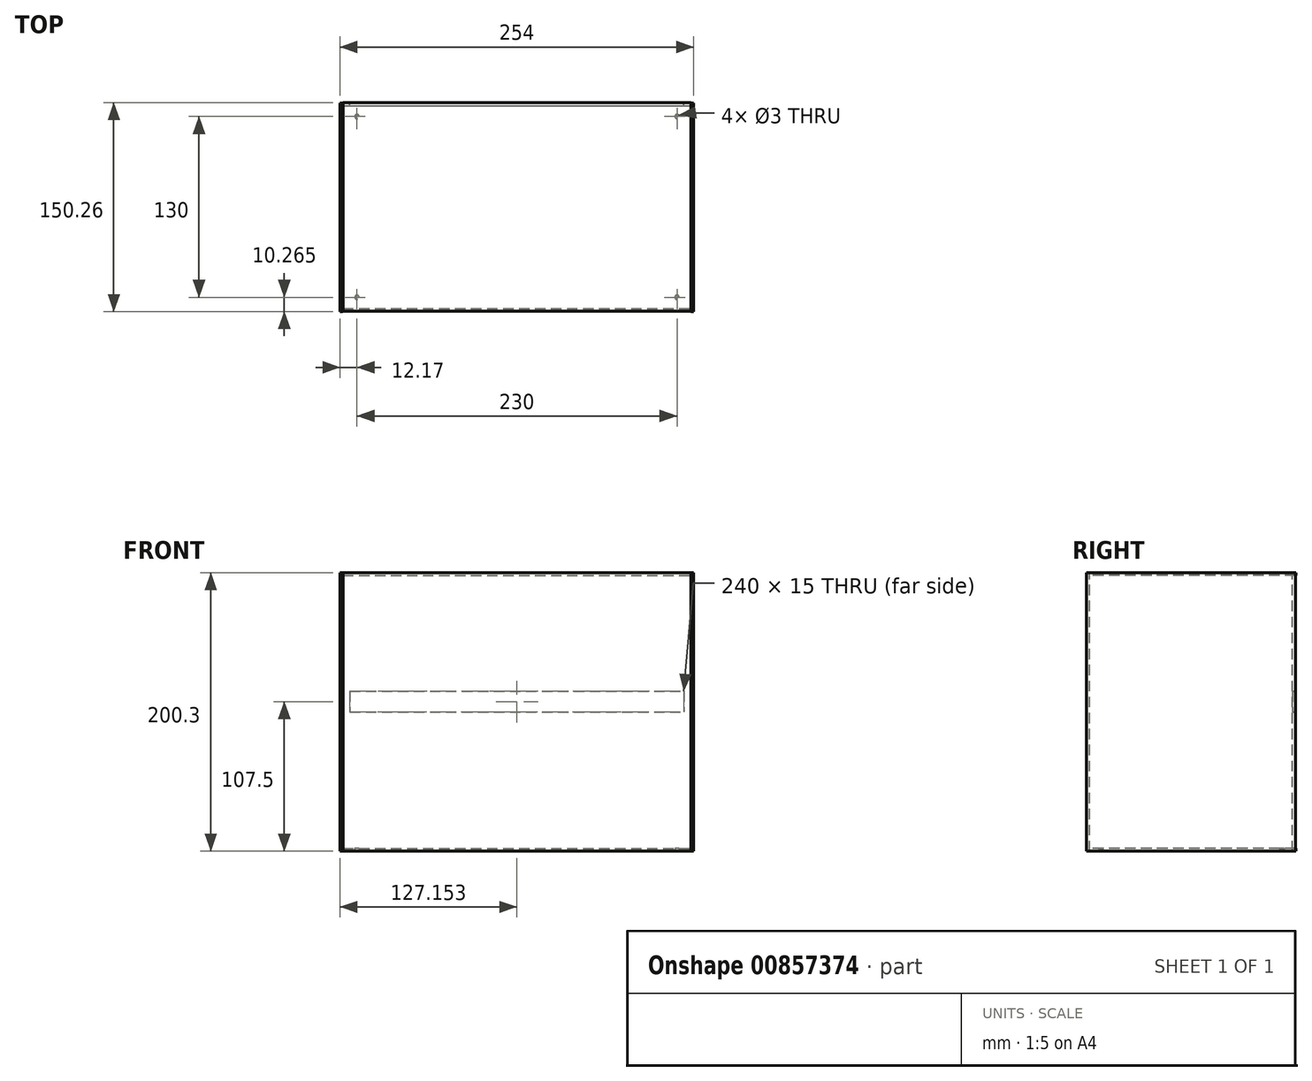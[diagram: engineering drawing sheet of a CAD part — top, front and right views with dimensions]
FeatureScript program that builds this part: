
annotation { "Feature Type Name" : "Feature", "Feature Type Description" : "" }
export const myFeature = defineFeature(function(context is Context, id is Id, definition is map)
    precondition{}
    {
        {
            var Q0;
            Q0=qCreatedBy(makeId("Top.planeOp"),FACE);
            var sketch = newSketch(context, id + "F0", { "sketchPlane" : qUnion([Q0])});
            skLineSegment(sketch, "E0.bottom", {"start": v(-126.83, 77.1) * mm, "end": v(123.17, 77.1) * mm});
            skLineSegment(sketch, "E0.top", {"start": v(-126.83, -72.9) * mm, "end": v(123.17, -72.9) * mm});
            skLineSegment(sketch, "E0.left", {"start": v(-126.83, 77.1) * mm, "end": v(-126.83, -72.9) * mm});
            skLineSegment(sketch, "E0.right", {"start": v(123.17, 77.1) * mm, "end": v(123.17, -72.9) * mm});
            skCircle(sketch, "E1", {"center": v(113.17, -62.9) * mm, "radius": 1.5 * mm});
            skCircle(sketch, "E2", {"center": v(113.17, 67.1) * mm, "radius": 1.5 * mm});
            skCircle(sketch, "E3", {"center": v(-116.83, 67.1) * mm, "radius": 1.5 * mm});
            skCircle(sketch, "E4", {"center": v(-116.83, -62.9) * mm, "radius": 1.5 * mm});
            skSolve(sketch);
        }
        {
            var Q0;
            Q0 = qSketchRegion(id + "F0", true);
            extrude(context, id + "F1", {"entities" : qUnion([Q0]), "depth" : 2 * mm, "offsetDistance" : 25 * mm});
        }
        {
            var Q0;
            Q0=qCreatedBy(makeId("Front.planeOp"),FACE);
            var sketch = newSketch(context, id + "F2", { "sketchPlane" : qUnion([Q0])});
            skLineSegment(sketch, "E5.bottom", {"start": v(-126.85, 0) * mm, "end": v(123.15, 0) * mm});
            skLineSegment(sketch, "E5.top", {"start": v(-126.85, 200) * mm, "end": v(123.15, 200) * mm});
            skLineSegment(sketch, "E5.left", {"start": v(-126.85, 0) * mm, "end": v(-126.85, 200) * mm});
            skLineSegment(sketch, "E5.right", {"start": v(123.15, 0) * mm, "end": v(123.15, 200) * mm});
            skLineSegment(sketch, "E6.bottom", {"start": v(-121.85, 115) * mm, "end": v(118.15, 115) * mm});
            skLineSegment(sketch, "E6.top", {"start": v(-121.85, 100) * mm, "end": v(118.15, 100) * mm});
            skLineSegment(sketch, "E6.left", {"start": v(-121.85, 115) * mm, "end": v(-121.85, 100) * mm});
            skLineSegment(sketch, "E6.right", {"start": v(118.15, 115) * mm, "end": v(118.15, 100) * mm});
            skSolve(sketch);
        }
        {
            var Q0;
            Q0 = qSketchRegion(id + "F2", true);
            extrude(context, id + "F3", {"entities" : qUnion([Q0]), "depth" : 2 * mm, "offsetDistance" : 25 * mm});
        }
        {
            var Q0;
            Q0=makeQuery(id+"F3.opExtrude","SWEPT_BODY",BODY,{"disambiguationData":[OSD([sQuery(id+"F2.wireOp",EDGE,"E5.bottom"),sQuery(id+"F2.wireOp",EDGE,"E5.top"),sQuery(id+"F2.wireOp",EDGE,"E5.left"),sQuery(id+"F2.wireOp",EDGE,"E5.right"),sQuery(id+"F2.wireOp",EDGE,"E6.bottom"),sQuery(id+"F2.wireOp",EDGE,"E6.top"),sQuery(id+"F2.wireOp",EDGE,"E6.left"),sQuery(id+"F2.wireOp",EDGE,"E6.right")])]});
            transform(context, id + "F4", {"entities" : qUnion([Q0]), "transformType" : TransformType.TRANSLATION_3D, "dx" : 0 * mm, "dy" : 76.8 * mm, "dz" : 0 * mm, "makeCopy" : false});
        }
        {
            var Q0;
            Q0 = qSketchRegion(id + "F2", true);
            var Q1;
            Q1=makeQuery(id+"F2.imprint","IMPRINT",FACE,{"disambiguationData":[TD([[makeQuery(id+"F2.imprint","IMPRINT",EDGE,{"derivedFrom":sQuery(id+"F2.wireOp",EDGE,"E6.bottom")}),-1.0]])]});
            extrude(context, id + "F5", {"entities" : qUnion([Q0, Q1]), "depth" : 2 * mm, "offsetDistance" : 25 * mm});
        }
        {
            var Q0;
            Q0=sQuery(id+"F0.wireOp",EDGE,"E0.top");
            cPoint(context, id + "F6", {"entities" : qUnion([Q0]), "parameter" : 0.5});
        }
        {
            var Q0;
            Q0=makeQuery(id+"F5.opExtrude","SWEPT_BODY",BODY,{"disambiguationData":[OSD([sQuery(id+"F2.wireOp",EDGE,"E5.bottom"),sQuery(id+"F2.wireOp",EDGE,"E5.top"),sQuery(id+"F2.wireOp",EDGE,"E5.left"),sQuery(id+"F2.wireOp",EDGE,"E5.right"),sQuery(id+"F2.wireOp",EDGE,"E6.bottom"),sQuery(id+"F2.wireOp",EDGE,"E6.top"),sQuery(id+"F2.wireOp",EDGE,"E6.left"),sQuery(id+"F2.wireOp",EDGE,"E6.right")])]});
            var Q1;
            Q1 = qCreatedBy(id + "F6" ,VERTEX);
            transform(context, id + "F7", {"entities" : qUnion([Q0]), "transformType" : TransformType.TRANSLATION_3D, "dx" : 0 * mm, "dy" : -71 * mm, "dz" : 0 * mm, "makeCopy" : false});
        }
        {
            var Q0;
            Q0=qCreatedBy(makeId("Right.planeOp"),FACE);
            var sketch = newSketch(context, id + "F8", { "sketchPlane" : qUnion([Q0])});
            skLineSegment(sketch, "E7.bottom", {"start": v(-73.16, 0) * mm, "end": v(76.84, 0) * mm});
            skLineSegment(sketch, "E7.top", {"start": v(-73.16, 200) * mm, "end": v(76.84, 200) * mm});
            skLineSegment(sketch, "E7.left", {"start": v(-73.16, 0) * mm, "end": v(-73.16, 200) * mm});
            skLineSegment(sketch, "E7.right", {"start": v(76.84, 0) * mm, "end": v(76.84, 200) * mm});
            skSolve(sketch);
        }
        {
            var Q0;
            Q0 = qSketchRegion(id + "F8", true);
            extrude(context, id + "F9", {"entities" : qUnion([Q0]), "depth" : 2 * mm, "offsetDistance" : 25 * mm});
        }
        {
            var Q0;
            Q0=makeQuery(id+"F9.opExtrude","SWEPT_BODY",BODY,{"disambiguationData":[OSD([sQuery(id+"F8.wireOp",EDGE,"E7.bottom"),sQuery(id+"F8.wireOp",EDGE,"E7.top"),sQuery(id+"F8.wireOp",EDGE,"E7.left"),sQuery(id+"F8.wireOp",EDGE,"E7.right")])]});
            transform(context, id + "F10", {"entities" : qUnion([Q0]), "transformType" : TransformType.TRANSLATION_3D, "dx" : 123 * mm, "dy" : 0 * mm, "dz" : 0 * mm, "makeCopy" : false});
        }
        {
            var Q0;
            Q0 = qSketchRegion(id + "F8", true);
            extrude(context, id + "F11", {"entities" : qUnion([Q0]), "depth" : 2 * mm, "offsetDistance" : 25 * mm});
        }
        {
            var Q0;
            Q0=makeQuery(id+"F11.opExtrude","SWEPT_BODY",BODY,{"disambiguationData":[OSD([sQuery(id+"F8.wireOp",EDGE,"E7.bottom"),sQuery(id+"F8.wireOp",EDGE,"E7.top"),sQuery(id+"F8.wireOp",EDGE,"E7.left"),sQuery(id+"F8.wireOp",EDGE,"E7.right")])]});
            transform(context, id + "F12", {"entities" : qUnion([Q0]), "transformType" : TransformType.TRANSLATION_3D, "dx" : -129 * mm, "dy" : 0 * mm, "dz" : 0 * mm, "makeCopy" : false});
        }
        {
            var Q0;
            Q0 = qSketchRegion(id + "F0", true);
            var Q1;
            Q1=makeQuery(id+"F0.imprint","IMPRINT",FACE,{"disambiguationData":[TD([[makeQuery(id+"F0.imprint","IMPRINT",EDGE,{"derivedFrom":sQuery(id+"F0.wireOp",EDGE,"E3")}),1.0]])]});
            var Q2;
            Q2=makeQuery(id+"F0.imprint","IMPRINT",FACE,{"disambiguationData":[TD([[makeQuery(id+"F0.imprint","IMPRINT",EDGE,{"derivedFrom":sQuery(id+"F0.wireOp",EDGE,"E4")}),1.0]])]});
            var Q3;
            Q3=makeQuery(id+"F0.imprint","IMPRINT",FACE,{"disambiguationData":[TD([[makeQuery(id+"F0.imprint","IMPRINT",EDGE,{"derivedFrom":sQuery(id+"F0.wireOp",EDGE,"E2")}),1.0]])]});
            var Q4;
            Q4=makeQuery(id+"F0.imprint","IMPRINT",FACE,{"disambiguationData":[TD([[makeQuery(id+"F0.imprint","IMPRINT",EDGE,{"derivedFrom":sQuery(id+"F0.wireOp",EDGE,"E1")}),1.0]])]});
            extrude(context, id + "F13", {"entities" : qUnion([Q0, Q1, Q2, Q3, Q4]), "depth" : 2 * mm, "offsetDistance" : 25 * mm});
        }
        {
            var Q0;
            Q0=makeQuery(id+"F13.opExtrude","SWEPT_BODY",BODY,{"disambiguationData":[OSD([sQuery(id+"F0.wireOp",EDGE,"E0.bottom"),sQuery(id+"F0.wireOp",EDGE,"E0.top"),sQuery(id+"F0.wireOp",EDGE,"E0.left"),sQuery(id+"F0.wireOp",EDGE,"E0.right"),sQuery(id+"F0.wireOp",EDGE,"E1"),sQuery(id+"F0.wireOp",EDGE,"E2"),sQuery(id+"F0.wireOp",EDGE,"E3"),sQuery(id+"F0.wireOp",EDGE,"E4")])]});
            transform(context, id + "F14", {"entities" : qUnion([Q0]), "transformType" : TransformType.TRANSLATION_3D, "dx" : 0 * mm, "dy" : 0 * mm, "dz" : 198.3 * mm, "makeCopy" : false});
        }
    });
